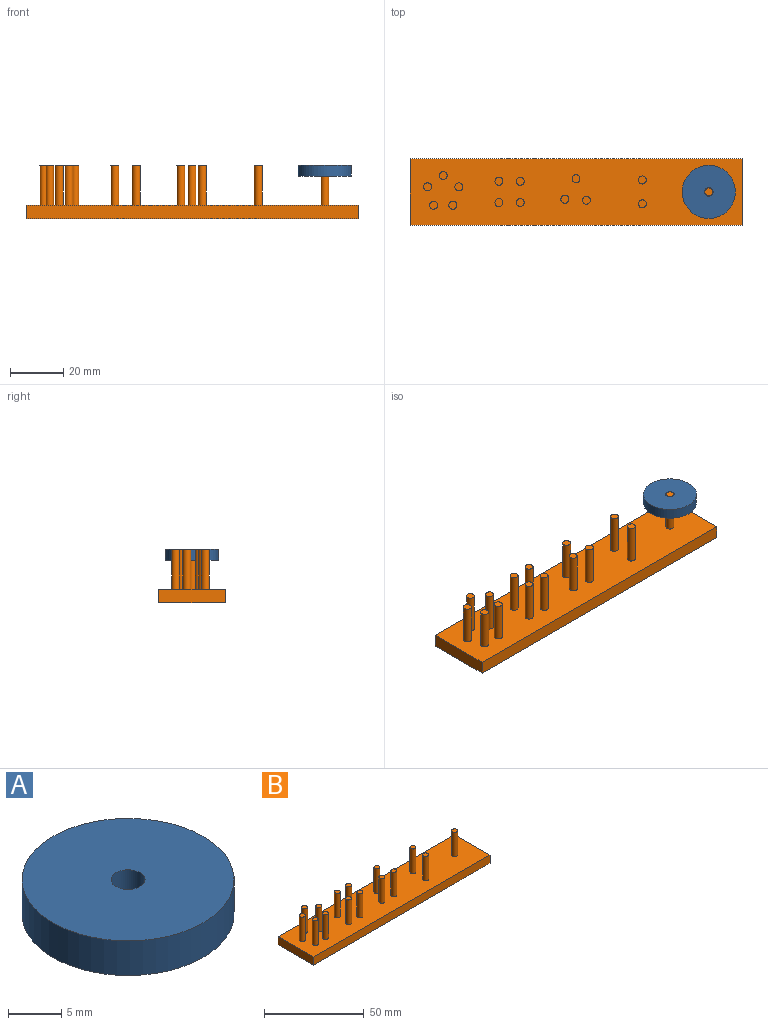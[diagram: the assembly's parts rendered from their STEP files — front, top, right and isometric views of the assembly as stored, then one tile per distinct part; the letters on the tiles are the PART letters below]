
ASSEMBLY  parts=2 mates=1
PART A: 4 faces, bbox 20x20x4 mm
  f0: cylinder r=10mm len=20mm, axis (0,0,1), area 251.3mm2, adj f1,f2
  f1: plane 20x20mm, normal (0,0,-1), area 306.1mm2, adj f0,f3
  f2: plane 20x20mm, normal (0,0,1), area 306.1mm2, adj f0,f3
  f3: cylinder r=1.6mm len=4mm, axis (0,0,1), area 40.2mm2, adj f1,f2
PART B: 36 faces, bbox 125x25x20 mm
  f0: plane 25x5mm, normal (1,0,0), area 125mm2, adj f1,f3,f4,f5
  f1: plane 125x5mm, normal (0,1,0), area 625mm2, adj f0,f2,f4,f5
  f2: plane 25x5mm, normal (-1,0,0), area 125mm2, adj f1,f3,f4,f5
  f3: plane 125x5mm, normal (0,-1,0), area 625mm2, adj f0,f2,f4,f5
  f4: plane 125x25mm, normal (0,0,1), area 3019mm2, adj f0,f1,f2,f3,f6,f8,f10,f12
  f5: plane 125x25mm, normal (0,0,-1), area 3125mm2, adj f0,f1,f2,f3
  f6: cylinder r=1.5mm len=15mm, axis (0,0,-1), area 141.4mm2, adj f4,f7
  f7: plane 3x3mm, normal (0,0,1), area 7.1mm2, adj f6
  f8: cylinder r=1.5mm len=15mm, axis (0,0,-1), area 141.4mm2, adj f4,f9
  f9: plane 3x3mm, normal (0,0,1), area 7.1mm2, adj f8
  f10: cylinder r=1.5mm len=15mm, axis (0,0,-1), area 141.4mm2, adj f4,f11
  f11: plane 3x3mm, normal (0,0,1), area 7.1mm2, adj f10
  f12: cylinder r=1.5mm len=15mm, axis (0,0,-1), area 141.4mm2, adj f4,f13
  f13: plane 3x3mm, normal (0,0,1), area 7.1mm2, adj f12
  f14: cylinder r=1.5mm len=15mm, axis (0,0,-1), area 141.4mm2, adj f4,f15
  f15: plane 3x3mm, normal (0,0,1), area 7.1mm2, adj f14
  f16: cylinder r=1.5mm len=15mm, axis (0,0,-1), area 141.4mm2, adj f4,f17
  f17: plane 3x3mm, normal (0,0,1), area 7.1mm2, adj f16
  f18: cylinder r=1.5mm len=15mm, axis (0,0,-1), area 141.4mm2, adj f4,f19
  f19: plane 3x3mm, normal (0,0,1), area 7.1mm2, adj f18
  f20: cylinder r=1.5mm len=15mm, axis (0,0,-1), area 141.4mm2, adj f4,f21
  f21: plane 3x3mm, normal (0,0,1), area 7.1mm2, adj f20
  f22: cylinder r=1.5mm len=15mm, axis (0,0,-1), area 141.4mm2, adj f4,f23
  f23: plane 3x3mm, normal (0,0,1), area 7.1mm2, adj f22
  f24: cylinder r=1.5mm len=15mm, axis (0,0,-1), area 141.4mm2, adj f4,f25
  f25: plane 3x3mm, normal (0,0,1), area 7.1mm2, adj f24
  f26: cylinder r=1.5mm len=15mm, axis (0,0,-1), area 141.4mm2, adj f4,f27
  f27: plane 3x3mm, normal (0,0,1), area 7.1mm2, adj f26
  f28: cylinder r=1.5mm len=15mm, axis (0,0,-1), area 141.4mm2, adj f4,f29
  f29: plane 3x3mm, normal (0,0,1), area 7.1mm2, adj f28
  f30: cylinder r=1.5mm len=15mm, axis (0,0,-1), area 141.4mm2, adj f4,f31
  f31: plane 3x3mm, normal (0,0,1), area 7.1mm2, adj f30
  f32: cylinder r=1.5mm len=15mm, axis (0,0,-1), area 141.4mm2, adj f4,f33
  f33: plane 3x3mm, normal (0,0,1), area 7.1mm2, adj f32
  f34: cylinder r=1.5mm len=15mm, axis (0,0,-1), area 141.4mm2, adj f4,f35
  f35: plane 3x3mm, normal (0,0,1), area 7.1mm2, adj f34
PLACE A t=(-22.07,-21.46,24.23)mm
PLACE B t=(-40.08,21.45,4.23)mm
MATE planar A.f0 <-> B.f6  axis (0,0,1) through (9.92,21.45,24.23)mm
